# Revit family: PRD_FrankeWS_WstBns_EXOSHygieneWasteBin_EXOS611EX_611EB_611EW
name_source: partatom
category: Specialty Equipment
revit_build: Autodesk Revit 2018 (Build: 20190510_1515(x64)
units: mm (PartAtom-declared; Revit-internal decimal feet)

## family parameters
Cut with Voids When Loaded = No
Host = Face
OmniClass Number = 23.40.20.31.11
OmniClass Title = Bins
Part Type = Normal
Room Calculation Point = No
Round Connector Dimension = Use Diameter
Shared = No

## types (3) — shared parameters
AssetType = Fixed
BagHolder = No
Category = Pr_40_50_07_96, Waste bins
Default Elevation = 600 mm
DispenserMaterial = PRD_AR_StainlessSteel_SatinFinished
DurationUnit = year
Features = stainless steel, surface satin finished
FillingVolume = 3.70 liter
Finish = satin finished
IfcExportAs = IfcFurnitureType
IfcExportType = USERDEFINED
IntegralAccessories = incl. mounting materials
IsBuiltIn = TRUE
Lid = Yes
Lock = No lock
MainColor = stainless steel
Manufacturer = KWC Group AG
ManufacturerName = KWC Group AG
ManufacturerURL = www.kwc.com
Material = stainless steel
MaterialCode = 1.4301
MaterialThickness = 1.20 mm
NBSDescription = Waste bins
NBSReference = 45-35-72/380
NominalDepth = 125 mm  [stored 0.410105 ft]
NominalHeight = 332 mm  [stored 1.08924 ft]
NominalWidth = 234 mm  [stored 0.767717 ft]
ProductInformation = https://pim.kwc.com
Size = 234 x 332 x 125 mm
Style = Waste bin
SurfaceTreatment = InoxPlus (anti fingerprint)
TailorMade = No
TypeOfFixing = Screw
TypeOfMounting = Recessed mounting
URL = www.kwc.com
Uniclass2015Code = Pr_40_50_07_96
Uniclass2015Title = Waste bins
Uniclass2015Version = Products v1.17
Version = 1
WarrantyDurationUnit = year

## per-type parameters (varying)
| type | BIMObjectName | Description | GrossWeight | ModelNumber | Name | NetWeight | PanelMaterial |
| EXOS611EX | PRD_AR_WasteBins_EXOSHygieneWasteBin_EXOS611EX | Hygiene waste bin for recessed mounting, stainless steel with satin finish and InoxPlus surface refinement for the reduction of finger marks and better cleaning characteristics (easy to clean), material thickness 1.2 mm, capacity approx. 3.7 litres, hinged self-closing front, integrated plastic container for waste removal, includes mounting materials. | 3.42 kg | 2030034630 | Hygiene Waste Bin EXOS611EX | 2.90 kg | PRD_AR_StainlessSteel_SatinFinished |
| EXOS611EB | PRD_AR_WasteBins_EXOSHygieneWasteBin_EXOS611EB | Hygiene waste bin for recessed mounting, stainless steel with satin finish, black safety glass front panel and casing with InoxPlus surface refinement for the reduction of finger marks and better cleaning characteristics (easy to clean), material thickness 1.2 mm, capacity approx. 3.7 litres, hinged self-closing front, integrated plastic container for waste removal, includes mounting materials. | 6.85 kg | 2030034631 | Hygiene Waste Bin EXOS611EB | 5.85 kg | PRD_AR_Glass_Black |
| EXOS611EW | PRD_AR_WasteBins_EXOSHygieneWasteBin_EXOS611EW | Hygiene waste bin for recessed mounting, stainless steel with satin finish, white safety glass front panel and casing with InoxPlus surface refinement for the reduction of finger marks and better cleaning characteristics (easy to clean), material thickness 1.2 mm, capacity approx. 3.7 litres, hinged self-closing front, integrated plastic container for waste removal, includes mounting materials. | 6.85 kg | 2030034665 | Hygiene Waste Bin EXOS611EW | 5.85 kg | PRD_AR_Glass_White |

note: column(s) folded — value = type name in every type: Model, ModelReference

note: [stored X ft] marks values corroborated as IEEE doubles in the binary element streams (Revit-internal decimal feet)

## geometry (parser evidence)
native form markers: Sweep x4
no freeform markers — native parametric forms only
